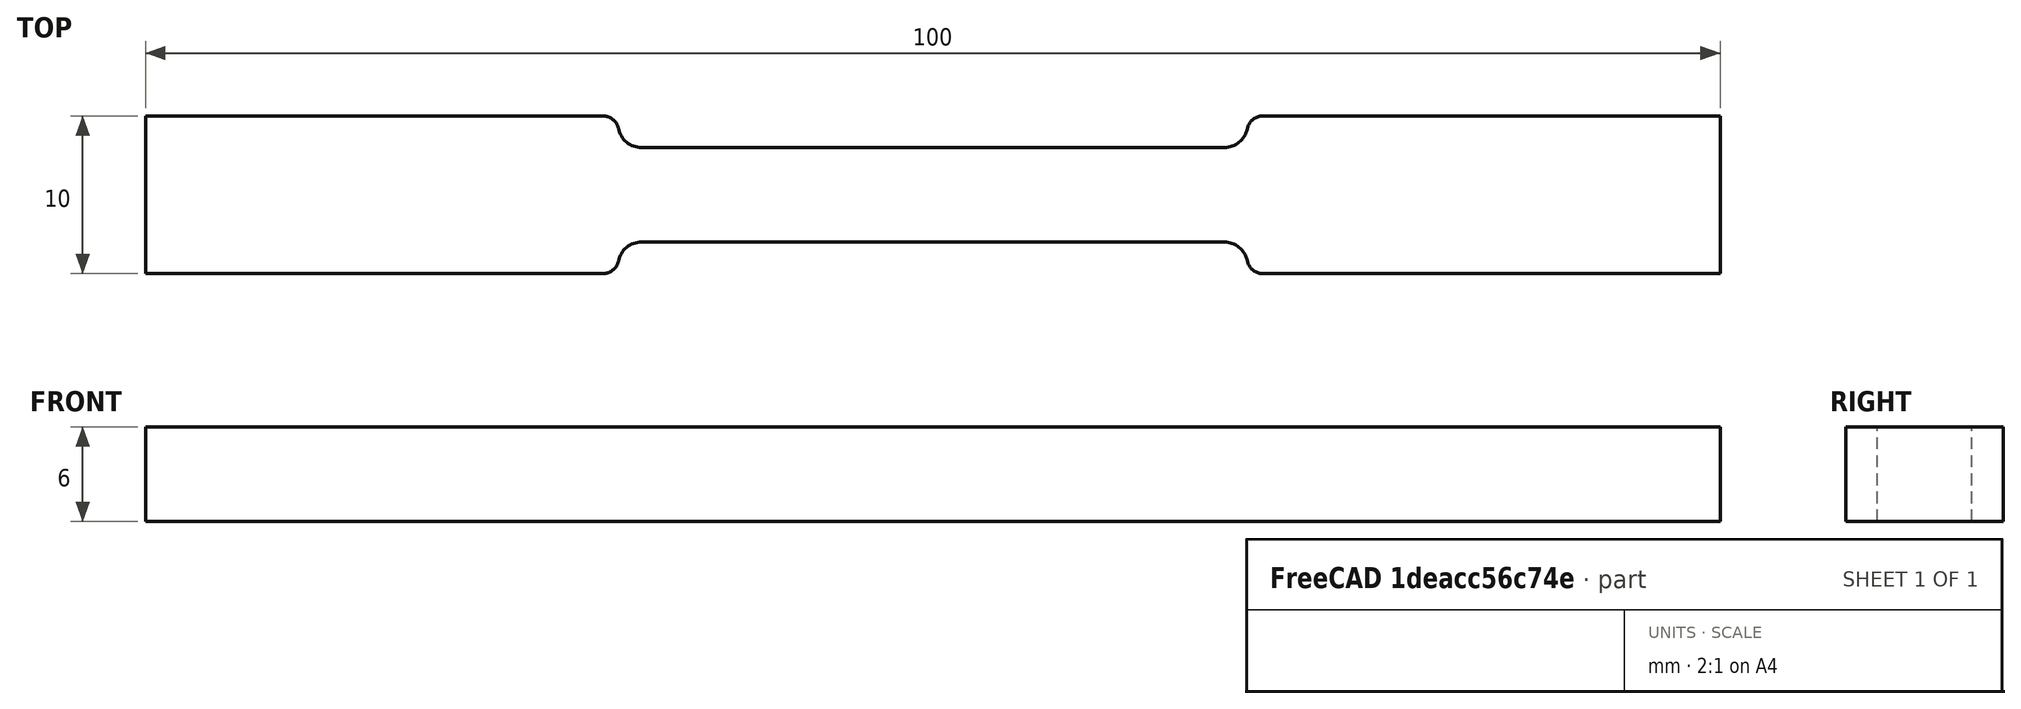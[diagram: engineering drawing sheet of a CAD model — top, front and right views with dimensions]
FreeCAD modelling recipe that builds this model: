
FCSTD DOCUMENT  (FreeCAD 0.19R)
Label: E8_6mm_ModFillet
License: All rights reserved
LicenseURL: http://en.wikipedia.org/wiki/All_rights_reserved
objects: PartDesign::Fillet×2, Sketcher::SketchObject×1, PartDesign::Pad×1, PartDesign::Body×1
note: 8 computed .brp shape members not serialized (recipe doc carries the construction recipe); baked Part::Feature solids carry a one-line shape summary decoded from their .brp

FEATURE [Sketcher::SketchObject] Sketch
  FullyConstrained = false
  MapMode = 5
  Support = -> [XY_Plane]
  sketch-geometry (33):
    g0: GeomPoint X=0 Y=10 Z=0
    g1: GeomPoint X=30 Y=10 Z=0
    g2: GeomPoint X=30 Y=8 Z=0
    g3: GeomPoint X=70 Y=8 Z=0
    g4: GeomPoint X=70 Y=10 Z=0
    g5: GeomPoint X=130 Y=0 Z=0
    g6: GeomPoint X=70 Y=2 Z=0
    g7: GeomPoint X=30 Y=0 Z=0
    g8: LineSegment StartX=0 StartY=0 StartZ=0 EndX=0 EndY=10 EndZ=0
    g9: LineSegment StartX=0 StartY=10 StartZ=0 EndX=30 EndY=10 EndZ=0
    g10: LineSegment StartX=30 StartY=10 StartZ=0 EndX=30 EndY=8 EndZ=0
    g11: LineSegment StartX=30 StartY=8 StartZ=0 EndX=70 EndY=8 EndZ=0
    g12: LineSegment StartX=70 StartY=8 StartZ=0 EndX=70 EndY=10 EndZ=0
    g13: LineSegment StartX=70 StartY=0 StartZ=0 EndX=70 EndY=2 EndZ=0
    g14: LineSegment StartX=30 StartY=2 StartZ=0 EndX=30 EndY=0 EndZ=0
    g15: LineSegment StartX=30 StartY=0 StartZ=0 EndX=0 EndY=0 EndZ=0
    g16: GeomPoint X=30 Y=2 Z=0
    g17: GeomPoint X=30 Y=2 Z=0
    g18: GeomPoint X=30 Y=2 Z=0
    g19: LineSegment StartX=30 StartY=2 StartZ=0 EndX=70 EndY=2 EndZ=0
    g20: GeomPoint X=30 Y=0 Z=0
    g21: GeomPoint X=30 Y=0 Z=0
    g22: GeomPoint X=30 Y=0 Z=0
    g23: GeomPoint X=30 Y=0 Z=0
    g24: GeomPoint X=30 Y=0 Z=0
    g25: GeomPoint X=75 Y=0 Z=0
    g26: GeomPoint X=75 Y=0 Z=0
    g27: GeomPoint X=30 Y=0 Z=0
    g28: GeomPoint X=30 Y=0 Z=0
    g29: GeomPoint X=30 Y=0 Z=0
    g30: LineSegment StartX=70 StartY=10 StartZ=0 EndX=100 EndY=10 EndZ=0
    g31: LineSegment StartX=100 StartY=10 StartZ=0 EndX=100 EndY=0 EndZ=0
    g32: LineSegment StartX=100 StartY=0 StartZ=0 EndX=70 EndY=0 EndZ=0
  constraints (54):
    c: PointOnObject(g5,g-1)
    c: Coincident(g8,g-1)
    c: Coincident(g8,g0)
    c: Coincident(g9,g8)
    c: Coincident(g9,g1)
    c: Coincident(g10,g9)
    c: Coincident(g10,g2)
    c: Coincident(g11,g10)
    c: Coincident(g11,g3)
    c: Coincident(g12,g11)
    c: Coincident(g12,g4)
    c: Coincident(g13,g6)
    c: Coincident(g14,g7)
    c: Coincident(g15,g8)
    c: Vertical(g8)
    c: Vertical(g10)
    c: Vertical(g14)
    c: Vertical(g13)
    c: Vertical(g12)
    c: Horizontal(g11)
    c: Coincident(g16,g14)
    c: Coincident(g17,g14)
    c: Coincident(g18,g14)
    c: Coincident(g19,g14)
    c: Coincident(g19,g13)
    c: Horizontal(g19)
    c: Horizontal(g9)
    c: DistanceY(g8,g8) = 10
    c: DistanceX(g9,g9) = 30
    c: Coincident(g20,g14)
    c: Coincident(g21,g15)
    c: Coincident(g22,g15)
    c: Coincident(g23,g15)
    c: Coincident(g24,g15)
    c: Coincident(g27,g14)
    c: Coincident(g28,g14)
    c: Coincident(g29,g15)
    c: Coincident(g14,g15)
    c: DistanceY(g14,g10) = 6
    c: Coincident(g30,g12)
    c: Horizontal(g30)
    c: Coincident(g31,g30)
    c: PointOnObject(g31,g-1)
    c: Vertical(g31)
    c: Coincident(g32,g31)
    c: Coincident(g32,g13)
    c: Horizontal(g32)
    c: Equal(g32,g30)
    c: Equal(g30,g15)
    c: Equal(g15,g9)
    c: DistanceX(g8,g30) = 100
    c: Equal(g8,g31)
    c: Equal(g10,g14)
    c: Horizontal(g15)
FEATURE [PartDesign::Pad] Pad
  Direction = (1,1,1)
  Length = 6
  Length2 = 100
  Profile = -> Sketch
  Type = 0
FEATURE [PartDesign::Fillet] Fillet
  Base = -> Pad [Edge17,Edge32,Edge1,Edge14]
  BaseFeature = -> Pad
  Radius = 1.5
  SupportTransform = false
FEATURE [PartDesign::Fillet] Fillet001
  Base = -> Fillet [Edge40,Edge3,Edge41,Edge47]
  BaseFeature = -> Fillet
  Radius = 1
  SupportTransform = false
FEATURE [PartDesign::Body] Body
  Group = -> [Sketch,Pad,Fillet,Fillet001]
  Origin = -> Origin
  Tip = -> Fillet001
